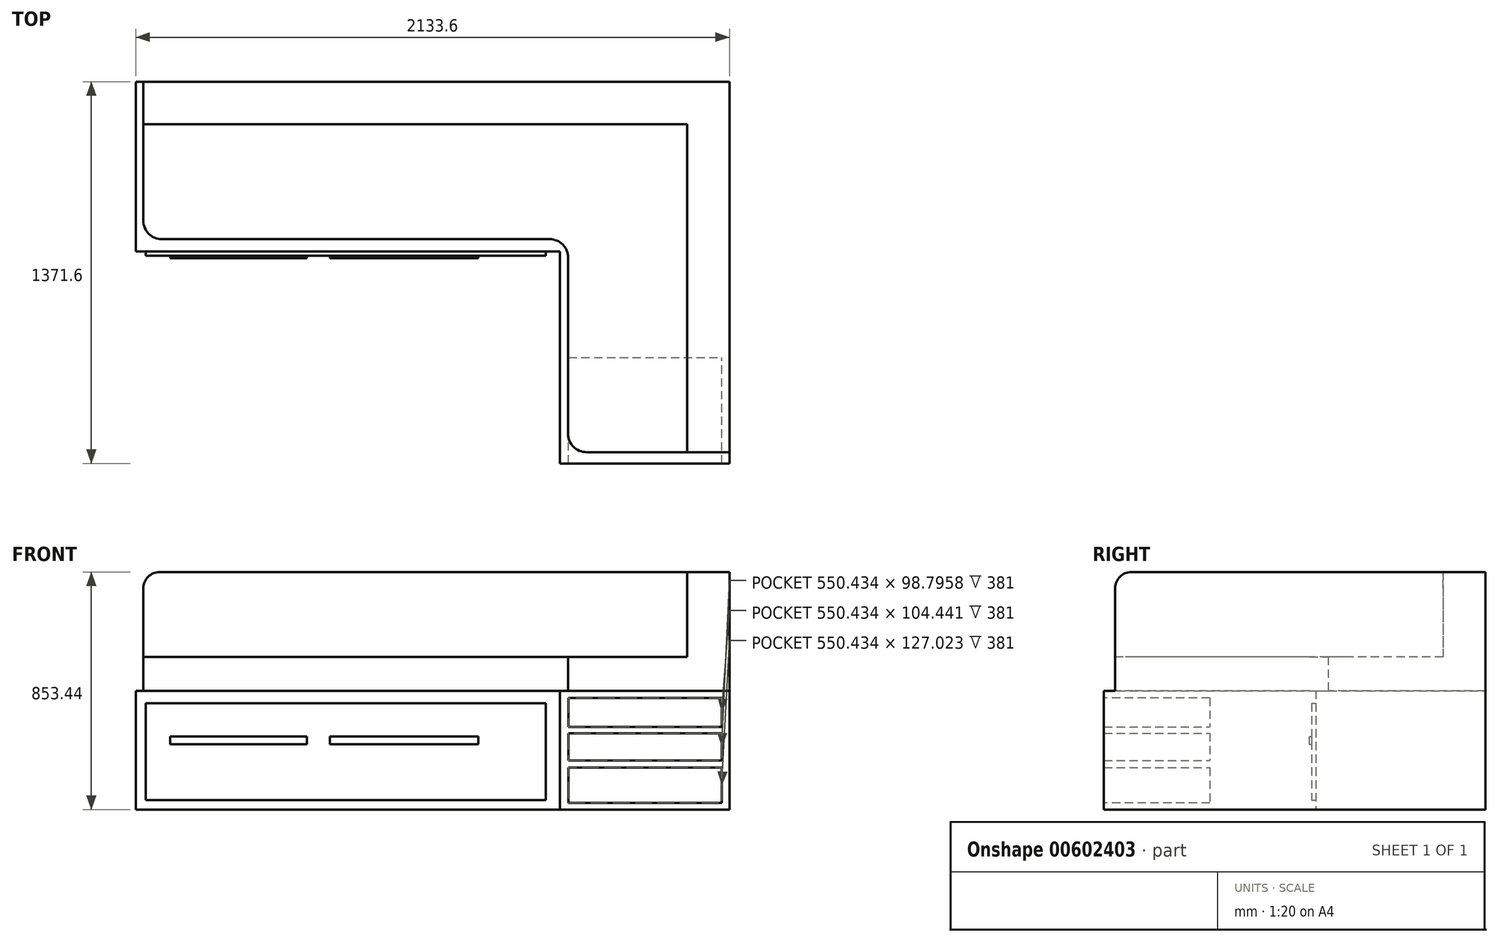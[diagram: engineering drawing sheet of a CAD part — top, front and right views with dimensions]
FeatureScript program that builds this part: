
annotation { "Feature Type Name" : "Feature", "Feature Type Description" : "" }
export const myFeature = defineFeature(function(context is Context, id is Id, definition is map)
    precondition{}
    {
        {
            var Q0;
            Q0=qCreatedBy(makeId("Top.planeOp"),FACE);
            var sketch = newSketch(context, id + "F0", { "sketchPlane" : qUnion([Q0])});
            skLineSegment(sketch, "E0", {"start": v(0, 0) * mm, "end": v(2133.6, 0) * mm});
            skLineSegment(sketch, "E1", {"start": v(2133.6, 0) * mm, "end": v(2133.6, -1371.6) * mm});
            skLineSegment(sketch, "E2", {"start": v(2133.6, -1371.6) * mm, "end": v(1524, -1371.6) * mm});
            skLineSegment(sketch, "E3", {"start": v(1524, -1371.6) * mm, "end": v(1524, -609.6) * mm});
            skLineSegment(sketch, "E4", {"start": v(1524, -609.6) * mm, "end": v(0, -609.6) * mm});
            skLineSegment(sketch, "E5", {"start": v(0, -609.6) * mm, "end": v(0, 0) * mm});
            skSolve(sketch);
        }
        {
            var Q0;
            Q0=makeQuery(id+"F0.imprint","IMPRINT",FACE,{"disambiguationData":[TD([[makeQuery(id+"F0.imprint","IMPRINT",EDGE,{"derivedFrom":sQuery(id+"F0.wireOp",EDGE,"E0")}),-1.0]])]});
            extrude(context, id + "F1", {"entities" : qUnion([Q0]), "depth" : 426.72 * mm, "offsetDistance" : 30.48 * mm});
        }
        {
            var Q0;
            Q0=makeQuery(id+"F1.opExtrude","CAP_FACE",FACE,{"disambiguationData":[OSD([sQuery(id+"F0.wireOp",EDGE,"E0"),sQuery(id+"F0.wireOp",EDGE,"E1"),sQuery(id+"F0.wireOp",EDGE,"E2"),sQuery(id+"F0.wireOp",EDGE,"E3"),sQuery(id+"F0.wireOp",EDGE,"E4"),sQuery(id+"F0.wireOp",EDGE,"E5")])],"isStart":false});
            var sketch = newSketch(context, id + "F2", { "sketchPlane" : qUnion([Q0])});
            skLineSegment(sketch, "E6", {"start": v(27.33, 0) * mm, "end": v(27.33, -566.01) * mm});
            skLineSegment(sketch, "E7", {"start": v(27.33, -566.01) * mm, "end": v(1553.56, -566.01) * mm});
            skLineSegment(sketch, "E8", {"start": v(1553.56, -566.01) * mm, "end": v(1553.56, -1331.26) * mm});
            skLineSegment(sketch, "E9", {"start": v(1553.56, -1331.26) * mm, "end": v(2133.6, -1331.26) * mm});
            skLineSegment(sketch, "E10", {"start": v(2133.6, -1331.26) * mm, "end": v(2133.6, 0) * mm});
            skLineSegment(sketch, "E11", {"start": v(2133.6, 0) * mm, "end": v(27.33, 0) * mm});
            skSolve(sketch);
        }
        {
            var Q0;
            Q0=makeQuery(id+"F2.imprint","IMPRINT",FACE,{"disambiguationData":[TD([[makeQuery(id+"F2.imprint","IMPRINT",EDGE,{"derivedFrom":sQuery(id+"F2.wireOp",EDGE,"E6")}),1.0]])]});
            extrude(context, id + "F3", {"entities" : qUnion([Q0]), "operationType" : NewBodyOperationType.ADD, "depth" : 121.92 * mm, "offsetDistance" : 30.48 * mm});
        }
        {
            var Q0;
            Q0=makeQuery(id+"F3.opExtrude","CAP_FACE",FACE,{"disambiguationData":[OSD([sQuery(id+"F2.wireOp",EDGE,"E6"),sQuery(id+"F2.wireOp",EDGE,"E7"),sQuery(id+"F2.wireOp",EDGE,"E8"),sQuery(id+"F2.wireOp",EDGE,"E9"),sQuery(id+"F2.wireOp",EDGE,"E10"),sQuery(id+"F2.wireOp",EDGE,"E11")])],"isStart":false});
            var sketch = newSketch(context, id + "F4", { "sketchPlane" : qUnion([Q0])});
            skLineSegment(sketch, "E12", {"start": v(27.33, 0) * mm, "end": v(27.33, -152.4) * mm});
            skLineSegment(sketch, "E13", {"start": v(27.33, -152.4) * mm, "end": v(1981.2, -152.4) * mm});
            skLineSegment(sketch, "E14", {"start": v(1981.2, -152.4) * mm, "end": v(1981.2, -1331.26) * mm});
            skLineSegment(sketch, "E15", {"start": v(1981.2, -1331.26) * mm, "end": v(2133.6, -1331.26) * mm});
            skLineSegment(sketch, "E16", {"start": v(2133.6, -1331.26) * mm, "end": v(2133.6, 0) * mm});
            skLineSegment(sketch, "E17", {"start": v(2133.6, 0) * mm, "end": v(27.33, 0) * mm});
            skSolve(sketch);
        }
        {
            var Q0;
            Q0=makeQuery(id+"F4.imprint","IMPRINT",FACE,{"disambiguationData":[TD([[makeQuery(id+"F4.imprint","IMPRINT",EDGE,{"derivedFrom":sQuery(id+"F4.wireOp",EDGE,"E12")}),1.0]])]});
            extrude(context, id + "F5", {"entities" : qUnion([Q0]), "operationType" : NewBodyOperationType.ADD, "depth" : 304.8 * mm, "offsetDistance" : 30.48 * mm});
        }
        {
            var Q0;
            Q0=makeQuery(id+"F3.opExtrude","SWEPT_EDGE",EDGE,{"disambiguationData":[OSD([sQuery(id+"F2.wireOp",EDGE,"E6"),sQuery(id+"F2.wireOp",EDGE,"E7")])]});
            var Q1;
            Q1=makeQuery(id+"F3.opExtrude","SWEPT_EDGE",EDGE,{"disambiguationData":[OSD([sQuery(id+"F2.wireOp",EDGE,"E7"),sQuery(id+"F2.wireOp",EDGE,"E8")])]});
            var Q2;
            Q2=makeQuery(id+"F3.opExtrude","SWEPT_EDGE",EDGE,{"disambiguationData":[OSD([sQuery(id+"F2.wireOp",EDGE,"E8"),sQuery(id+"F2.wireOp",EDGE,"E9")])]});
            fillet(context, id + "F6", {"entities" : qUnion([Q0, Q1, Q2]), "radius" : 66.23 * mm, "tangentPropagation" : true, "allowEdgeOverflow" : false});
        }
        {
            var Q0;
            Q0=makeQuery(id+"F5.opExtrude","CAP_EDGE",EDGE,{"disambiguationData":[OSD([sQuery(id+"F4.wireOp",EDGE,"E12")])],"isStart":false});
            var Q1;
            Q1=makeQuery(id+"F5.opExtrude","CAP_EDGE",EDGE,{"disambiguationData":[OSD([sQuery(id+"F4.wireOp",EDGE,"E15")])],"isStart":false});
            fillet(context, id + "F7", {"entities" : qUnion([Q0, Q1]), "radius" : 58.87 * mm, "tangentPropagation" : true, "allowEdgeOverflow" : false});
        }
        {
            var Q0;
            Q0=makeQuery(id+"F1.opExtrude","SWEPT_FACE",FACE,{"disambiguationData":[OSD([sQuery(id+"F0.wireOp",EDGE,"E4")])]});
            var sketch = newSketch(context, id + "F8", { "sketchPlane" : qUnion([Q0])});
            skLineSegment(sketch, "E18.bottom", {"start": v(36.5, 381.55) * mm, "end": v(1473.28, 381.55) * mm});
            skLineSegment(sketch, "E18.top", {"start": v(36.5, 34.35) * mm, "end": v(1473.28, 34.35) * mm});
            skLineSegment(sketch, "E18.left", {"start": v(36.5, 381.55) * mm, "end": v(36.5, 34.35) * mm});
            skLineSegment(sketch, "E18.right", {"start": v(1473.28, 381.55) * mm, "end": v(1473.28, 34.35) * mm});
            skSolve(sketch);
        }
        {
            var Q0;
            Q0=makeQuery(id+"F8.imprint","IMPRINT",FACE,{"disambiguationData":[TD([[makeQuery(id+"F8.imprint","IMPRINT",EDGE,{"derivedFrom":sQuery(id+"F8.wireOp",EDGE,"E18.bottom")}),-1.0]])]});
            extrude(context, id + "F9", {"entities" : qUnion([Q0]), "operationType" : NewBodyOperationType.ADD, "depth" : 15.24 * mm, "offsetDistance" : 30.48 * mm});
        }
        {
            var Q0;
            Q0=makeQuery(id+"F9.opExtrude","CAP_FACE",FACE,{"disambiguationData":[OSD([sQuery(id+"F8.wireOp",EDGE,"E18.bottom"),sQuery(id+"F8.wireOp",EDGE,"E18.top"),sQuery(id+"F8.wireOp",EDGE,"E18.left"),sQuery(id+"F8.wireOp",EDGE,"E18.right")])],"isStart":false});
            var sketch = newSketch(context, id + "F10", { "sketchPlane" : qUnion([Q0])});
            skLineSegment(sketch, "E19.bottom", {"start": v(124.01, 263) * mm, "end": v(615.17, 263) * mm});
            skLineSegment(sketch, "E19.top", {"start": v(124.01, 234.76) * mm, "end": v(615.17, 234.76) * mm});
            skLineSegment(sketch, "E19.left", {"start": v(124.01, 263) * mm, "end": v(124.01, 234.76) * mm});
            skLineSegment(sketch, "E19.right", {"start": v(615.17, 263) * mm, "end": v(615.17, 234.76) * mm});
            skLineSegment(sketch, "E20.bottom", {"start": v(697.03, 263) * mm, "end": v(1230.53, 263) * mm});
            skLineSegment(sketch, "E20.top", {"start": v(697.03, 234.76) * mm, "end": v(1230.53, 234.76) * mm});
            skLineSegment(sketch, "E20.left", {"start": v(697.03, 263) * mm, "end": v(697.03, 234.76) * mm});
            skLineSegment(sketch, "E20.right", {"start": v(1230.53, 263) * mm, "end": v(1230.53, 234.76) * mm});
            skSolve(sketch);
        }
        {
            var Q0;
            Q0=makeQuery(id+"F10.imprint","IMPRINT",FACE,{"disambiguationData":[TD([[makeQuery(id+"F10.imprint","IMPRINT",EDGE,{"derivedFrom":sQuery(id+"F10.wireOp",EDGE,"E19.bottom")}),-1.0]])]});
            var Q1;
            Q1=makeQuery(id+"F10.imprint","IMPRINT",FACE,{"disambiguationData":[TD([[makeQuery(id+"F10.imprint","IMPRINT",EDGE,{"derivedFrom":sQuery(id+"F10.wireOp",EDGE,"E20.bottom")}),-1.0]])]});
            extrude(context, id + "F11", {"entities" : qUnion([Q0, Q1]), "operationType" : NewBodyOperationType.ADD, "depth" : 9.14 * mm, "offsetDistance" : 30.48 * mm});
        }
        {
            var Q0;
            Q0=makeQuery(id+"F1.opExtrude","SWEPT_FACE",FACE,{"disambiguationData":[OSD([sQuery(id+"F0.wireOp",EDGE,"E2")])]});
            var sketch = newSketch(context, id + "F12", { "sketchPlane" : qUnion([Q0])});
            skLineSegment(sketch, "E21.bottom", {"start": v(1555.14, 401.3) * mm, "end": v(2105.57, 401.3) * mm});
            skLineSegment(sketch, "E21.top", {"start": v(1555.14, 23.06) * mm, "end": v(2105.57, 23.06) * mm});
            skLineSegment(sketch, "E21.left", {"start": v(1555.14, 401.3) * mm, "end": v(1555.14, 23.06) * mm});
            skLineSegment(sketch, "E21.right", {"start": v(2105.57, 401.3) * mm, "end": v(2105.57, 23.06) * mm});
            skSolve(sketch);
        }
        {
            var Q0;
            Q0=makeQuery(id+"F12.imprint","IMPRINT",FACE,{"disambiguationData":[TD([[makeQuery(id+"F12.imprint","IMPRINT",EDGE,{"derivedFrom":sQuery(id+"F12.wireOp",EDGE,"E21.bottom")}),-1.0]])]});
            extrude(context, id + "F13", {"entities" : qUnion([Q0]), "operationType" : NewBodyOperationType.REMOVE, "oppositeDirection" : true, "depth" : 381 * mm, "offsetDistance" : 30.48 * mm});
        }
        {
            var Q0;
            Q0=makeQuery(id+"F13.boolean.opBoolean","COPY",FACE,{"derivedFrom":makeQuery(id+"F13.opExtrude","CAP_FACE",FACE,{"disambiguationData":[OSD([sQuery(id+"F12.wireOp",EDGE,"E21.bottom"),sQuery(id+"F12.wireOp",EDGE,"E21.top"),sQuery(id+"F12.wireOp",EDGE,"E21.left"),sQuery(id+"F12.wireOp",EDGE,"E21.right")])],"isStart":false})});
            var sketch = newSketch(context, id + "F14", { "sketchPlane" : qUnion([Q0])});
            skLineSegment(sketch, "E22.bottom", {"start": v(1555.14, 296.86) * mm, "end": v(2105.57, 296.86) * mm});
            skLineSegment(sketch, "E22.top", {"start": v(1555.14, 274.28) * mm, "end": v(2105.57, 274.28) * mm});
            skLineSegment(sketch, "E22.left", {"start": v(1555.14, 296.86) * mm, "end": v(1555.14, 274.28) * mm});
            skLineSegment(sketch, "E22.right", {"start": v(2105.57, 296.86) * mm, "end": v(2105.57, 274.28) * mm});
            skLineSegment(sketch, "E23.bottom", {"start": v(1555.14, 175.49) * mm, "end": v(2105.57, 175.49) * mm});
            skLineSegment(sketch, "E23.top", {"start": v(1555.14, 150.08) * mm, "end": v(2105.57, 150.08) * mm});
            skLineSegment(sketch, "E23.left", {"start": v(1555.14, 175.49) * mm, "end": v(1555.14, 150.08) * mm});
            skLineSegment(sketch, "E23.right", {"start": v(2105.57, 175.49) * mm, "end": v(2105.57, 150.08) * mm});
            skSolve(sketch);
        }
        {
            var Q0;
            Q0=makeQuery(id+"F14.imprint","IMPRINT",FACE,{"disambiguationData":[TD([[makeQuery(id+"F14.imprint","IMPRINT",EDGE,{"derivedFrom":sQuery(id+"F14.wireOp",EDGE,"E22.bottom")}),-1.0]])]});
            var Q1;
            Q1=makeQuery(id+"F14.imprint","IMPRINT",FACE,{"disambiguationData":[TD([[makeQuery(id+"F14.imprint","IMPRINT",EDGE,{"derivedFrom":sQuery(id+"F14.wireOp",EDGE,"E23.bottom")}),-1.0]])]});
            extrude(context, id + "F15", {"entities" : qUnion([Q0, Q1]), "operationType" : NewBodyOperationType.ADD, "depth" : 381 * mm, "offsetDistance" : 30.48 * mm});
        }
    });
